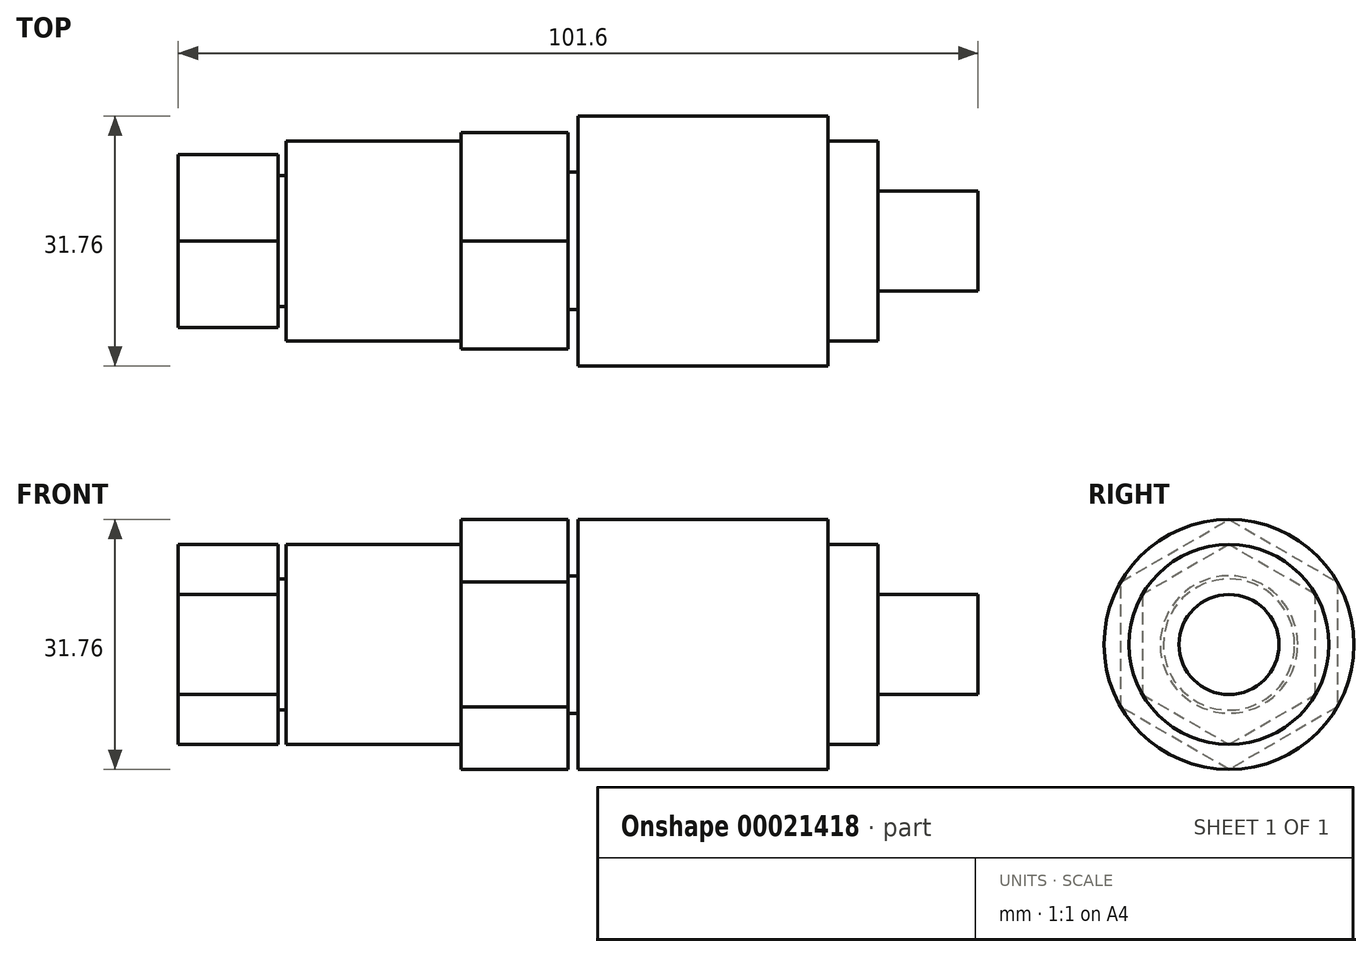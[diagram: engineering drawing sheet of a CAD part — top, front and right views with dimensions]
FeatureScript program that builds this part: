
annotation { "Feature Type Name" : "Feature", "Feature Type Description" : "" }
export const myFeature = defineFeature(function(context is Context, id is Id, definition is map)
    precondition{}
    {
        {
            var Q0;
            Q0=qCreatedBy(makeId("Front.planeOp"),FACE);
            var sketch = newSketch(context, id + "F0", { "sketchPlane" : qUnion([Q0])});
            skLineSegment(sketch, "E0", {"start": v(0, 0) * mm, "end": v(101.6, 0) * mm});
            skLineSegment(sketch, "E1", {"start": v(101.6, 0) * mm, "end": v(101.6, 6.35) * mm});
            skLineSegment(sketch, "E2", {"start": v(101.6, 6.35) * mm, "end": v(88.9, 6.35) * mm});
            skLineSegment(sketch, "E3", {"start": v(88.9, 6.35) * mm, "end": v(88.9, 12.7) * mm});
            skLineSegment(sketch, "E4", {"start": v(88.9, 12.7) * mm, "end": v(82.55, 12.7) * mm});
            skLineSegment(sketch, "E5", {"start": v(82.55, 12.7) * mm, "end": v(82.55, 15.88) * mm});
            skLineSegment(sketch, "E6", {"start": v(82.55, 15.88) * mm, "end": v(50.8, 15.87) * mm});
            skLineSegment(sketch, "E7", {"start": v(50.8, 15.87) * mm, "end": v(50.8, 8.73) * mm});
            skLineSegment(sketch, "E8", {"start": v(50.8, 8.73) * mm, "end": v(49.53, 8.73) * mm});
            skLineSegment(sketch, "E9", {"start": v(49.53, 8.73) * mm, "end": v(49.53, 15.88) * mm});
            skLineSegment(sketch, "E10", {"start": v(49.53, 15.88) * mm, "end": v(35.94, 15.88) * mm});
            skLineSegment(sketch, "E11", {"start": v(35.94, 15.88) * mm, "end": v(35.94, 12.7) * mm});
            skLineSegment(sketch, "E12", {"start": v(35.94, 12.7) * mm, "end": v(13.72, 12.7) * mm});
            skLineSegment(sketch, "E13", {"start": v(13.72, 12.7) * mm, "end": v(13.72, 8.34) * mm});
            skLineSegment(sketch, "E14", {"start": v(13.72, 8.34) * mm, "end": v(12.7, 8.34) * mm});
            skLineSegment(sketch, "E15", {"start": v(12.7, 8.34) * mm, "end": v(12.7, 12.7) * mm});
            skLineSegment(sketch, "E16", {"start": v(12.7, 12.7) * mm, "end": v(0, 12.7) * mm});
            skLineSegment(sketch, "E17", {"start": v(0, 12.7) * mm, "end": v(0, 0) * mm});
            skLineSegment(sketch, "E18", {"start": v(82.55, 12.7) * mm, "end": v(82.55, 0) * mm, "construction": true});
            skLineSegment(sketch, "E19", {"start": v(40.93, 15.88) * mm, "end": v(40.93, 0) * mm, "construction": true});
            skLineSegment(sketch, "E20", {"start": v(28.02, 12.7) * mm, "end": v(28.02, 0) * mm, "construction": true});
            skSolve(sketch);
        }
        {
            var Q0;
            Q0=makeQuery(id+"F0.imprint","IMPRINT",FACE,{"disambiguationData":[TD([[makeQuery(id+"F0.imprint","IMPRINT",EDGE,{"derivedFrom":sQuery(id+"F0.wireOp",EDGE,"E0")}),1.0]])]});
            var Q1;
            Q1=sQuery(id+"F0.wireOp",EDGE,"E0");
            revolve(context, id + "F1", {"entities" : qUnion([Q0]), "axis" : qUnion([Q1]), "revolveType" : RevolveType.FULL});
        }
        {
            var Q0;
            Q0=makeQuery(id+"F1.opRevolve","SWEPT_FACE",FACE,{"disambiguationData":[OSD([sQuery(id+"F0.wireOp",EDGE,"E17")])]});
            var sketch = newSketch(context, id + "F2", { "sketchPlane" : qUnion([Q0])});
            skCircle(sketch, "E21.cCircle", {"center": v(0, 0) * mm, "radius": 12.7 * mm, "construction": true});
            skLineSegment(sketch, "E21.0", {"start": v(0, -12.7) * mm, "end": v(-11, -6.35) * mm});
            skLineSegment(sketch, "E21.1", {"start": v(-11, -6.35) * mm, "end": v(-11, 6.35) * mm});
            skLineSegment(sketch, "E21.2", {"start": v(-11, 6.35) * mm, "end": v(0, 12.7) * mm});
            skLineSegment(sketch, "E21.3", {"start": v(0, 12.7) * mm, "end": v(11, 6.35) * mm});
            skLineSegment(sketch, "E21.4", {"start": v(11, 6.35) * mm, "end": v(11, -6.35) * mm});
            skLineSegment(sketch, "E21.5", {"start": v(11, -6.35) * mm, "end": v(0, -12.7) * mm});
            skSolve(sketch);
        }
        {
            var Q0;
            {var subQ1=sQuery(id+"F2.wireOp",EDGE,"E21.5");Q0=makeQuery(id+"F2.imprint","IMPRINT",FACE,{"disambiguationData":[TD([[makeQuery(id+"F2.imprint","IMPRINT",EDGE,{"derivedFrom":subQ1}),1.0]])]});}
            var Q1;
            {var subQ1=sQuery(id+"F2.wireOp",EDGE,"E21.0");Q1=makeQuery(id+"F2.imprint","IMPRINT",FACE,{"disambiguationData":[TD([[makeQuery(id+"F2.imprint","IMPRINT",EDGE,{"derivedFrom":subQ1}),1.0]])]});}
            var Q2;
            {var subQ1=sQuery(id+"F2.wireOp",EDGE,"E21.1");Q2=makeQuery(id+"F2.imprint","IMPRINT",FACE,{"disambiguationData":[TD([[makeQuery(id+"F2.imprint","IMPRINT",EDGE,{"derivedFrom":subQ1}),1.0]])]});}
            var Q3;
            {var subQ1=sQuery(id+"F2.wireOp",EDGE,"E21.2");Q3=makeQuery(id+"F2.imprint","IMPRINT",FACE,{"disambiguationData":[TD([[makeQuery(id+"F2.imprint","IMPRINT",EDGE,{"derivedFrom":subQ1}),1.0]])]});}
            var Q4;
            {var subQ1=sQuery(id+"F2.wireOp",EDGE,"E21.3");Q4=makeQuery(id+"F2.imprint","IMPRINT",FACE,{"disambiguationData":[TD([[makeQuery(id+"F2.imprint","IMPRINT",EDGE,{"derivedFrom":subQ1}),1.0]])]});}
            var Q5;
            {var subQ1=sQuery(id+"F2.wireOp",EDGE,"E21.4");Q5=makeQuery(id+"F2.imprint","IMPRINT",FACE,{"disambiguationData":[TD([[makeQuery(id+"F2.imprint","IMPRINT",EDGE,{"derivedFrom":subQ1}),1.0]])]});}
            var Q6;
            Q6=makeQuery(id+"F1.opRevolve","SWEPT_FACE",FACE,{"disambiguationData":[OSD([sQuery(id+"F0.wireOp",EDGE,"E15")])]});
            extrude(context, id + "F3", {"entities" : qUnion([Q0, Q1, Q2, Q3, Q4, Q5]), "operationType" : NewBodyOperationType.REMOVE, "endBound" : BoundingType.UP_TO_SURFACE, "oppositeDirection" : true, "endBoundEntityFace" : qUnion([Q6]), "depth" : 11.43 * mm});
        }
        {
            var Q0;
            Q0=makeQuery(id+"F1.opRevolve","SWEPT_FACE",FACE,{"disambiguationData":[OSD([sQuery(id+"F0.wireOp",EDGE,"E11")])]});
            var sketch = newSketch(context, id + "F4", { "sketchPlane" : qUnion([Q0])});
            skCircle(sketch, "E22.cCircle", {"center": v(0, 0) * mm, "radius": 15.88 * mm, "construction": true});
            skLineSegment(sketch, "E22.0", {"start": v(0, -15.88) * mm, "end": v(-13.75, -7.94) * mm});
            skLineSegment(sketch, "E22.1", {"start": v(-13.75, -7.94) * mm, "end": v(-13.75, 7.94) * mm});
            skLineSegment(sketch, "E22.2", {"start": v(-13.75, 7.94) * mm, "end": v(0, 15.88) * mm});
            skLineSegment(sketch, "E22.3", {"start": v(0, 15.88) * mm, "end": v(13.75, 7.94) * mm});
            skLineSegment(sketch, "E22.4", {"start": v(13.75, 7.94) * mm, "end": v(13.75, -7.94) * mm});
            skLineSegment(sketch, "E22.5", {"start": v(13.75, -7.94) * mm, "end": v(0, -15.88) * mm});
            skLineSegment(sketch, "E23", {"start": v(0, 0) * mm, "end": v(0, -31.75) * mm, "construction": true});
            skSolve(sketch);
        }
        {
            var Q0;
            {var subQ1=sQuery(id+"F4.wireOp",EDGE,"E22.0");Q0=makeQuery(id+"F4.imprint","IMPRINT",FACE,{"disambiguationData":[TD([[makeQuery(id+"F4.imprint","IMPRINT",EDGE,{"derivedFrom":subQ1}),1.0]])]});}
            var Q1;
            {var subQ1=sQuery(id+"F4.wireOp",EDGE,"E22.1");Q1=makeQuery(id+"F4.imprint","IMPRINT",FACE,{"disambiguationData":[TD([[makeQuery(id+"F4.imprint","IMPRINT",EDGE,{"derivedFrom":subQ1}),1.0]])]});}
            var Q2;
            {var subQ1=sQuery(id+"F4.wireOp",EDGE,"E22.5");Q2=makeQuery(id+"F4.imprint","IMPRINT",FACE,{"disambiguationData":[TD([[makeQuery(id+"F4.imprint","IMPRINT",EDGE,{"derivedFrom":subQ1}),1.0]])]});}
            var Q3;
            {var subQ1=sQuery(id+"F4.wireOp",EDGE,"E22.4");Q3=makeQuery(id+"F4.imprint","IMPRINT",FACE,{"disambiguationData":[TD([[makeQuery(id+"F4.imprint","IMPRINT",EDGE,{"derivedFrom":subQ1}),1.0]])]});}
            var Q4;
            {var subQ1=sQuery(id+"F4.wireOp",EDGE,"E22.2");Q4=makeQuery(id+"F4.imprint","IMPRINT",FACE,{"disambiguationData":[TD([[makeQuery(id+"F4.imprint","IMPRINT",EDGE,{"derivedFrom":subQ1}),1.0]])]});}
            var Q5;
            {var subQ1=sQuery(id+"F4.wireOp",EDGE,"E22.3");Q5=makeQuery(id+"F4.imprint","IMPRINT",FACE,{"disambiguationData":[TD([[makeQuery(id+"F4.imprint","IMPRINT",EDGE,{"derivedFrom":subQ1}),1.0]])]});}
            var Q6;
            Q6=makeQuery(id+"F1.opRevolve","SWEPT_FACE",FACE,{"disambiguationData":[OSD([sQuery(id+"F0.wireOp",EDGE,"E9")])]});
            extrude(context, id + "F5", {"entities" : qUnion([Q0, Q1, Q2, Q3, Q4, Q5]), "operationType" : NewBodyOperationType.REMOVE, "endBound" : BoundingType.UP_TO_SURFACE, "oppositeDirection" : true, "endBoundEntityFace" : qUnion([Q6]), "depth" : 25.4 * mm});
        }
    });
